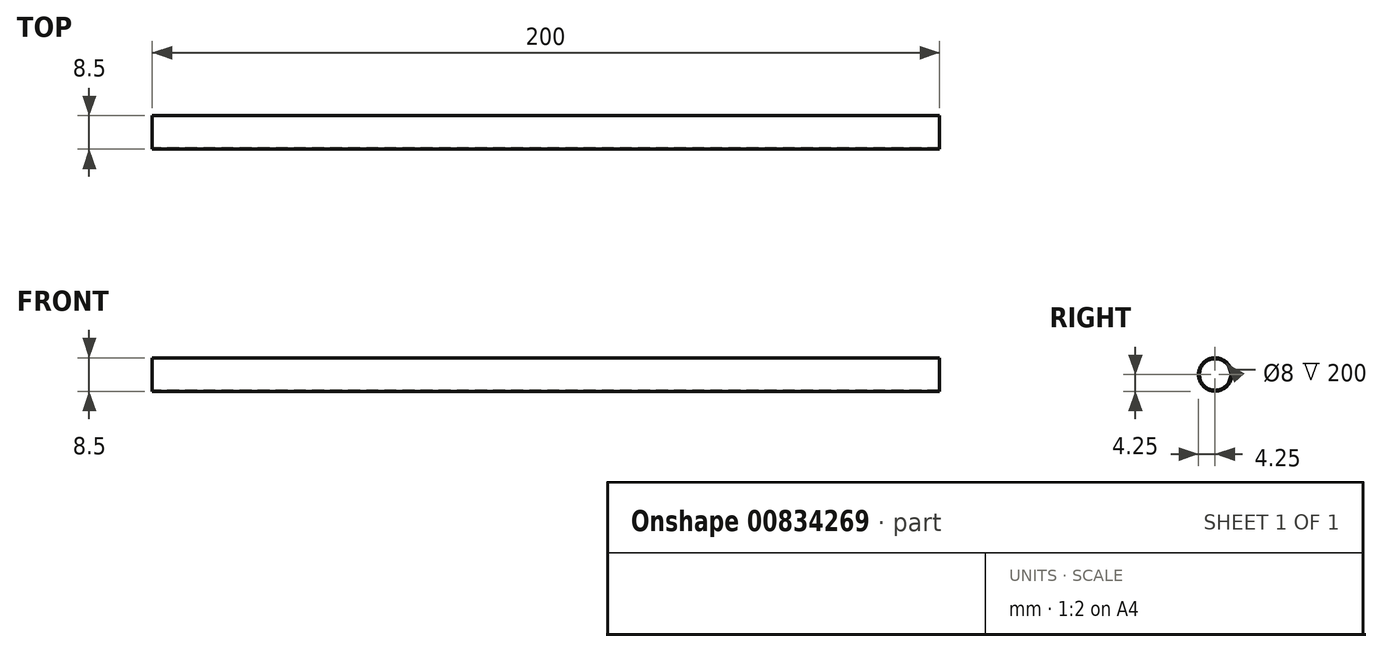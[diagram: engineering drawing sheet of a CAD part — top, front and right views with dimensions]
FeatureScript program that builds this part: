
annotation { "Feature Type Name" : "Feature", "Feature Type Description" : "" }
export const myFeature = defineFeature(function(context is Context, id is Id, definition is map)
    precondition{}
    {
        {
            var Q0;
            Q0=qCreatedBy(makeId("Right.planeOp"),FACE);
            var sketch = newSketch(context, id + "F0", { "sketchPlane" : qUnion([Q0])});
            skCircle(sketch, "E0", {"center": v(0, 0) * mm, "radius": 4.25 * mm});
            skCircle(sketch, "E1", {"center": v(0, 0) * mm, "radius": 4 * mm});
            skSolve(sketch);
        }
        {
            var Q0;
            Q0=makeQuery(id+"F0.imprint","IMPRINT",FACE,{"disambiguationData":[TD([[makeQuery(id+"F0.imprint","IMPRINT",EDGE,{"derivedFrom":sQuery(id+"F0.wireOp",EDGE,"E0")}),1.0]])]});
            extrude(context, id + "F1", {"entities" : qUnion([Q0]), "depth" : 200 * mm, "offsetDistance" : 25 * mm});
        }
    });
